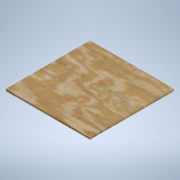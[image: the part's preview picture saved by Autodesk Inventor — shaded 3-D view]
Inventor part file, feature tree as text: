
AUTODESK INVENTOR PART (.ipt)
format: ipt  version: 2021.1 (Build 251245000, 245)  size: 112,640 bytes
history: native  units: mm
features: other x3, extrude x1, sketch x1, reference x1
ambient origin geometry x8: Origin, YZ Plane, XZ Plane, XY Plane, X Axis, Y Axis, Z Axis, Center Point
bodies: Solid1 (feature_tree)
feature tree (6):
  extrude  "Extrusion1"  [1 undecoded]
  sketch  "Sketch1"  dims[d2=270.0mm d3=0.0mm]
  reference  "Reference1"
  other  "<userpath>\Documents\Kerbal Kontroller\v.3.iam"
  other  "v.3.iam"
  other  "Sides:1"
note: 1 required parameter value undecoded (feature->parameter linkage not recoverable at this tier; creation-order binding heuristic only, values carry confidence <= 0.55)
